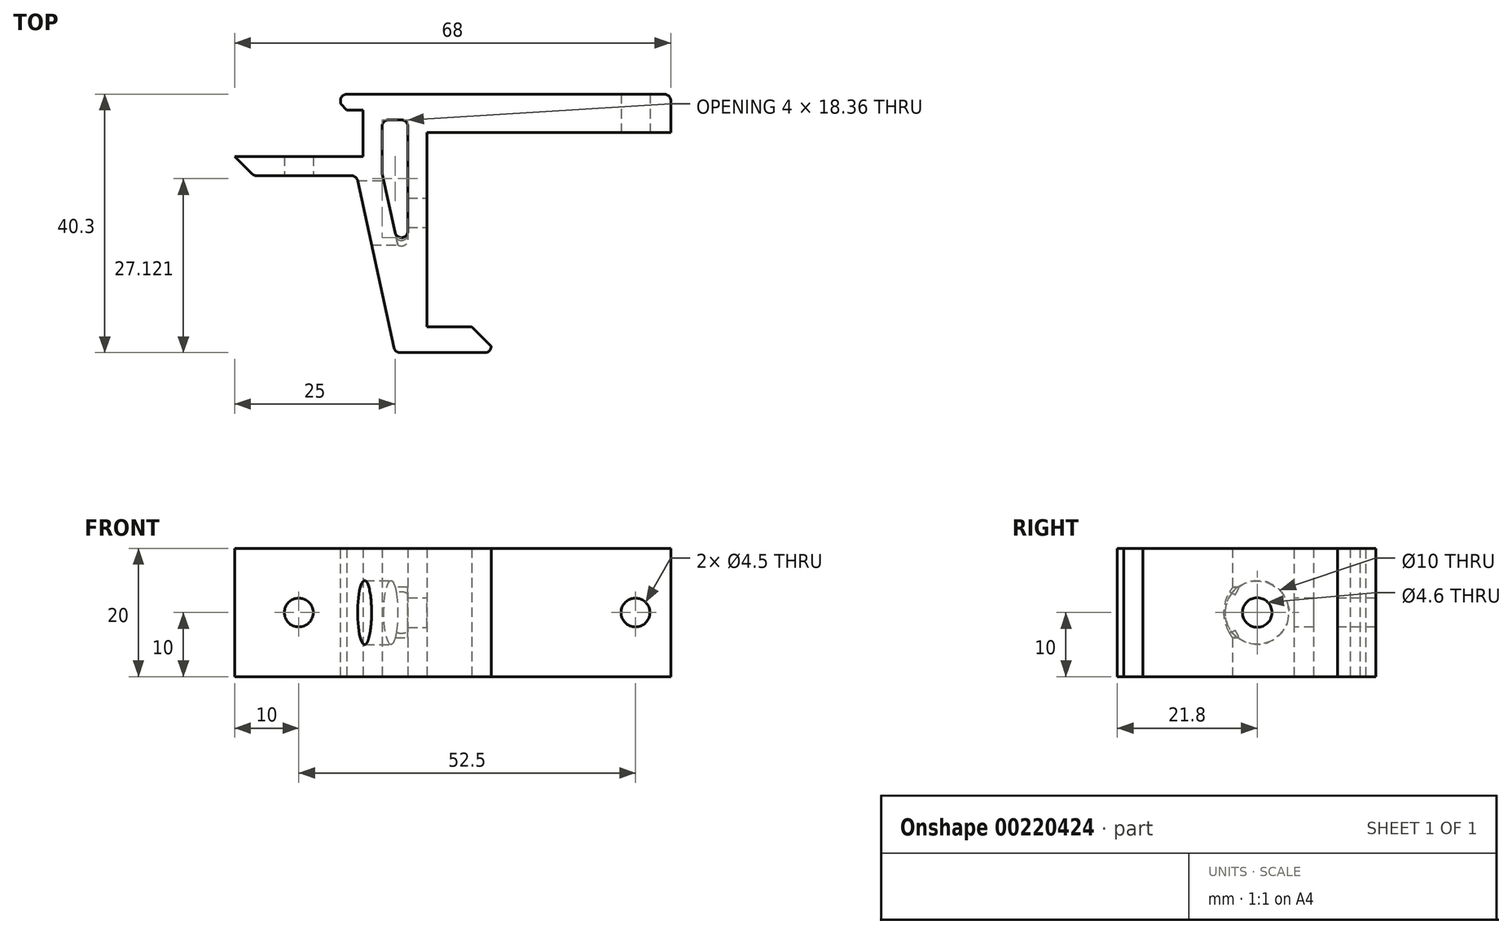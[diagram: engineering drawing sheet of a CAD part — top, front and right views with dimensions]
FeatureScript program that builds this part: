
annotation { "Feature Type Name" : "Feature", "Feature Type Description" : "" }
export const myFeature = defineFeature(function(context is Context, id is Id, definition is map)
    precondition{}
    {
        {
            var Q0;
            Q0=qCreatedBy(makeId("Top.planeOp"),FACE);
            var sketch = newSketch(context, id + "F0", { "sketchPlane" : qUnion([Q0])});
            skPoint(sketch, "E0.0", {"position": v(-10, -10) * mm});
            skPoint(sketch, "E1.0", {"position": v(10, -10) * mm});
            skLineSegment(sketch, "E2", {"start": v(-10, -10) * mm, "end": v(-10, -13) * mm});
            skLineSegment(sketch, "E3", {"start": v(-10, -13) * mm, "end": v(15, -13) * mm, "construction": true});
            skLineSegment(sketch, "E4", {"start": v(15, -13) * mm, "end": v(15, -40.6) * mm, "construction": true});
            skLineSegment(sketch, "E5", {"start": v(15, -40.6) * mm, "end": v(30, -40.6) * mm});
            skLineSegment(sketch, "E6", {"start": v(30, -40.6) * mm, "end": v(30, -36.6) * mm});
            skLineSegment(sketch, "E7", {"start": v(30, -36.6) * mm, "end": v(20, -36.6) * mm});
            skLineSegment(sketch, "E8", {"start": v(20, -36.6) * mm, "end": v(20, -6.3) * mm});
            skLineSegment(sketch, "E9", {"start": v(20, -6.3) * mm, "end": v(58, -6.3) * mm});
            skLineSegment(sketch, "E10", {"start": v(-10, -10) * mm, "end": v(10, -10) * mm});
            skLineSegment(sketch, "E11", {"start": v(10, -2.8) * mm, "end": v(8.5, -2.8) * mm});
            skLineSegment(sketch, "E12", {"start": v(6.5, -2.8) * mm, "end": v(6.5, -0.3) * mm});
            skLineSegment(sketch, "E13", {"start": v(6.5, -0.3) * mm, "end": v(58, -0.3) * mm});
            skLineSegment(sketch, "E14", {"start": v(58, -0.3) * mm, "end": v(58, -6.3) * mm});
            skLineSegment(sketch, "E15", {"start": v(15, -40.6) * mm, "end": v(9, -13) * mm});
            skLineSegment(sketch, "E16", {"start": v(-10, -13) * mm, "end": v(9, -13) * mm});
            skLineSegment(sketch, "E17", {"start": v(17, -4.3) * mm, "end": v(17, -30.97) * mm});
            skLineSegment(sketch, "E18", {"start": v(10, -2.8) * mm, "end": v(10, -10) * mm});
            skLineSegment(sketch, "E19", {"start": v(17, -4.3) * mm, "end": v(13, -4.3) * mm});
            skLineSegment(sketch, "E20", {"start": v(13, -4.3) * mm, "end": v(13, -12.57) * mm});
            skLineSegment(sketch, "E21", {"start": v(13, -12.57) * mm, "end": v(17, -30.97) * mm});
            skLineSegment(sketch, "E22", {"start": v(8.5, -2.8) * mm, "end": v(6.5, -2.8) * mm});
            skSolve(sketch);
        }
        {
            var Q0;
            Q0=makeQuery(id+"F0.imprint","IMPRINT",FACE,{"disambiguationData":[TD([[makeQuery(id+"F0.imprint","IMPRINT",EDGE,{"derivedFrom":sQuery(id+"F0.wireOp",EDGE,"E2")}),1.0]])]});
            extrude(context, id + "F1", {"entities" : qUnion([Q0]), "depth" : 20 * mm});
        }
        {
            var Q0;
            Q0=makeQuery(id+"F1.opExtrude","SWEPT_FACE",FACE,{"disambiguationData":[OSD([sQuery(id+"F0.wireOp",EDGE,"E9")])]});
            var sketch = newSketch(context, id + "F2", { "sketchPlane" : qUnion([Q0])});
            skLineSegment(sketch, "E23", {"start": v(20, 10) * mm, "end": v(58, 10) * mm, "construction": true});
            skCircle(sketch, "E24", {"center": v(52.5, 10) * mm, "radius": 2.25 * mm});
            skSolve(sketch);
        }
        {
            var Q0;
            Q0=makeQuery(id+"F1.opExtrude","SWEPT_FACE",FACE,{"disambiguationData":[OSD([sQuery(id+"F0.wireOp",EDGE,"E16")])]});
            var sketch = newSketch(context, id + "F3", { "sketchPlane" : qUnion([Q0])});
            skLineSegment(sketch, "E25", {"start": v(0, 20) * mm, "end": v(0, 0) * mm, "construction": true});
            skCircle(sketch, "E26", {"center": v(0, 10) * mm, "radius": 2.25 * mm});
            skSolve(sketch);
        }
        {
            var Q0;
            Q0=makeQuery(id+"F3.imprint","IMPRINT",FACE,{"disambiguationData":[TD([[makeQuery(id+"F3.imprint","IMPRINT",EDGE,{"derivedFrom":sQuery(id+"F3.wireOp",EDGE,"E26")}),1.0]])]});
            var Q1;
            Q1=makeQuery(id+"F2.imprint","IMPRINT",FACE,{"disambiguationData":[TD([[makeQuery(id+"F2.imprint","IMPRINT",EDGE,{"derivedFrom":sQuery(id+"F2.wireOp",EDGE,"E24")}),1.0]])]});
            extrude(context, id + "F4", {"entities" : qUnion([Q0, Q1]), "operationType" : NewBodyOperationType.REMOVE, "endBound" : BoundingType.UP_TO_NEXT, "oppositeDirection" : true, "depth" : 25 * mm});
        }
        {
            var Q0;
            Q0=makeQuery(id+"F1.opExtrude","SWEPT_FACE",FACE,{"disambiguationData":[OSD([sQuery(id+"F0.wireOp",EDGE,"E8")])]});
            var sketch = newSketch(context, id + "F5", { "sketchPlane" : qUnion([Q0])});
            skLineSegment(sketch, "E27", {"start": v(-18.8, 20) * mm, "end": v(-18.8, 0) * mm, "construction": true});
            skCircle(sketch, "E28", {"center": v(-18.8, 10) * mm, "radius": 2.3 * mm});
            skCircle(sketch, "E29", {"center": v(-18.8, 10) * mm, "radius": 5 * mm});
            skSolve(sketch);
        }
        {
            var Q0;
            Q0=makeQuery(id+"F5.imprint","IMPRINT",FACE,{"disambiguationData":[TD([[makeQuery(id+"F5.imprint","IMPRINT",EDGE,{"derivedFrom":sQuery(id+"F5.wireOp",EDGE,"E28")}),-1.0]])]});
            var Q1;
            Q1=makeQuery(id+"F1.opExtrude","SWEPT_FACE",FACE,{"disambiguationData":[OSD([sQuery(id+"F0.wireOp",EDGE,"E15")])]});
            var Q2;
            Q2=makeQuery(id+"F1.opExtrude","SWEPT_FACE",FACE,{"disambiguationData":[OSD([sQuery(id+"F0.wireOp",EDGE,"E17")])]});
            extrude(context, id + "F6", {"entities" : qUnion([Q0]), "operationType" : NewBodyOperationType.REMOVE, "endBound" : BoundingType.UP_TO_SURFACE, "oppositeDirection" : true, "endBoundEntityFace" : qUnion([Q1]), "depth" : 25 * mm, "hasSecondDirection" : true, "secondDirectionBound" : SecondDirectionBoundingType.UP_TO_SURFACE, "secondDirectionOppositeDirection" : true, "secondDirectionBoundEntityFace" : qUnion([Q2]), "secondDirectionDepth" : 25 * mm});
        }
        {
            var Q0;
            Q0=makeQuery(id+"F5.imprint","IMPRINT",FACE,{"disambiguationData":[TD([[makeQuery(id+"F5.imprint","IMPRINT",EDGE,{"derivedFrom":sQuery(id+"F5.wireOp",EDGE,"E28")}),1.0]])]});
            extrude(context, id + "F7", {"entities" : qUnion([Q0]), "operationType" : NewBodyOperationType.REMOVE, "endBound" : BoundingType.THROUGH_ALL, "oppositeDirection" : true, "depth" : 25 * mm});
        }
        {
            var Q0;
            Q0=makeQuery(id+"F1.opExtrude","SWEPT_EDGE",EDGE,{"disambiguationData":[OSD([sQuery(id+"F0.wireOp",EDGE,"E2"),sQuery(id+"F0.wireOp",EDGE,"E16")])]});
            var Q1;
            Q1=makeQuery(id+"F1.opExtrude","SWEPT_EDGE",EDGE,{"disambiguationData":[OSD([sQuery(id+"F0.wireOp",EDGE,"E6"),sQuery(id+"F0.wireOp",EDGE,"E7")])]});
            chamfer(context, id + "F8", {"entities" : qUnion([Q0, Q1]), "width" : 3 * mm, "tangentPropagation" : true});
        }
        {
            var Q0;
            Q0=makeQuery(id+"F1.opExtrude","SWEPT_EDGE",EDGE,{"disambiguationData":[OSD([sQuery(id+"F0.wireOp",EDGE,"E5"),sQuery(id+"F0.wireOp",EDGE,"E15")])]});
            var Q1;
            Q1=makeQuery(id+"F1.opExtrude","SWEPT_EDGE",EDGE,{"disambiguationData":[OSD([sQuery(id+"F0.wireOp",EDGE,"E5"),sQuery(id+"F0.wireOp",EDGE,"E6")])]});
            var Q2;
            Q2=makeQuery(id+"F1.opExtrude","SWEPT_EDGE",EDGE,{"disambiguationData":[OSD([sQuery(id+"F0.wireOp",EDGE,"E19"),sQuery(id+"F0.wireOp",EDGE,"E20")])]});
            var Q3;
            Q3=makeQuery(id+"F1.opExtrude","SWEPT_EDGE",EDGE,{"disambiguationData":[OSD([sQuery(id+"F0.wireOp",EDGE,"E17"),sQuery(id+"F0.wireOp",EDGE,"E19")])]});
            var Q4;
            Q4=makeQuery(id+"F1.opExtrude","SWEPT_EDGE",EDGE,{"disambiguationData":[OSD([sQuery(id+"F0.wireOp",EDGE,"E20"),sQuery(id+"F0.wireOp",EDGE,"E21")])]});
            var Q5;
            Q5=makeQuery(id+"F1.opExtrude","SWEPT_EDGE",EDGE,{"disambiguationData":[OSD([sQuery(id+"F0.wireOp",EDGE,"E17"),sQuery(id+"F0.wireOp",EDGE,"E21")])]});
            var Q6;
            Q6=makeQuery(id+"F1.opExtrude","SWEPT_EDGE",EDGE,{"disambiguationData":[OSD([sQuery(id+"F0.wireOp",EDGE,"E12"),sQuery(id+"F0.wireOp",EDGE,"E13")])]});
            var Q7;
            Q7=makeQuery(id+"F1.opExtrude","SWEPT_EDGE",EDGE,{"disambiguationData":[OSD([sQuery(id+"F0.wireOp",EDGE,"E13"),sQuery(id+"F0.wireOp",EDGE,"E14")])]});
            var Q8;
            Q8=makeQuery(id+"F1.opExtrude","SWEPT_EDGE",EDGE,{"disambiguationData":[OSD([sQuery(id+"F0.wireOp",EDGE,"E15"),sQuery(id+"F0.wireOp",EDGE,"E16")])]});
            var Q9;
            {var subQ0=sQuery(id+"F0.wireOp",EDGE,"E16");Q9=makeQuery(id+"F8.opChamfer","BLEND_EDGE",EDGE,{"blendedFrom":[makeQuery(id+"F1.opExtrude","SWEPT_EDGE",EDGE,{"disambiguationData":[OSD([sQuery(id+"F0.wireOp",EDGE,"E2"),subQ0])]}),makeQuery(id+"F1.opExtrude","SWEPT_FACE",FACE,{"disambiguationData":[OSD([subQ0])]})],"blendedInto":[makeQuery(id+"F1.opExtrude","SWEPT_FACE",FACE,{"disambiguationData":[OSD([subQ0])]})]});}
            fillet(context, id + "F9", {"entities" : qUnion([Q0, Q1, Q2, Q3, Q4, Q5, Q6, Q7, Q8, Q9]), "radius" : 1 * mm, "tangentPropagation" : true, "allowEdgeOverflow" : false});
        }
        {
            var Q0;
            Q0=makeQuery(id+"F1.opExtrude","SWEPT_EDGE",EDGE,{"disambiguationData":[OSD([sQuery(id+"F0.wireOp",EDGE,"E12"),sQuery(id+"F0.wireOp",EDGE,"E22")])]});
            chamfer(context, id + "F10", {"entities" : qUnion([Q0]), "width" : 1 * mm, "tangentPropagation" : true});
        }
    });
